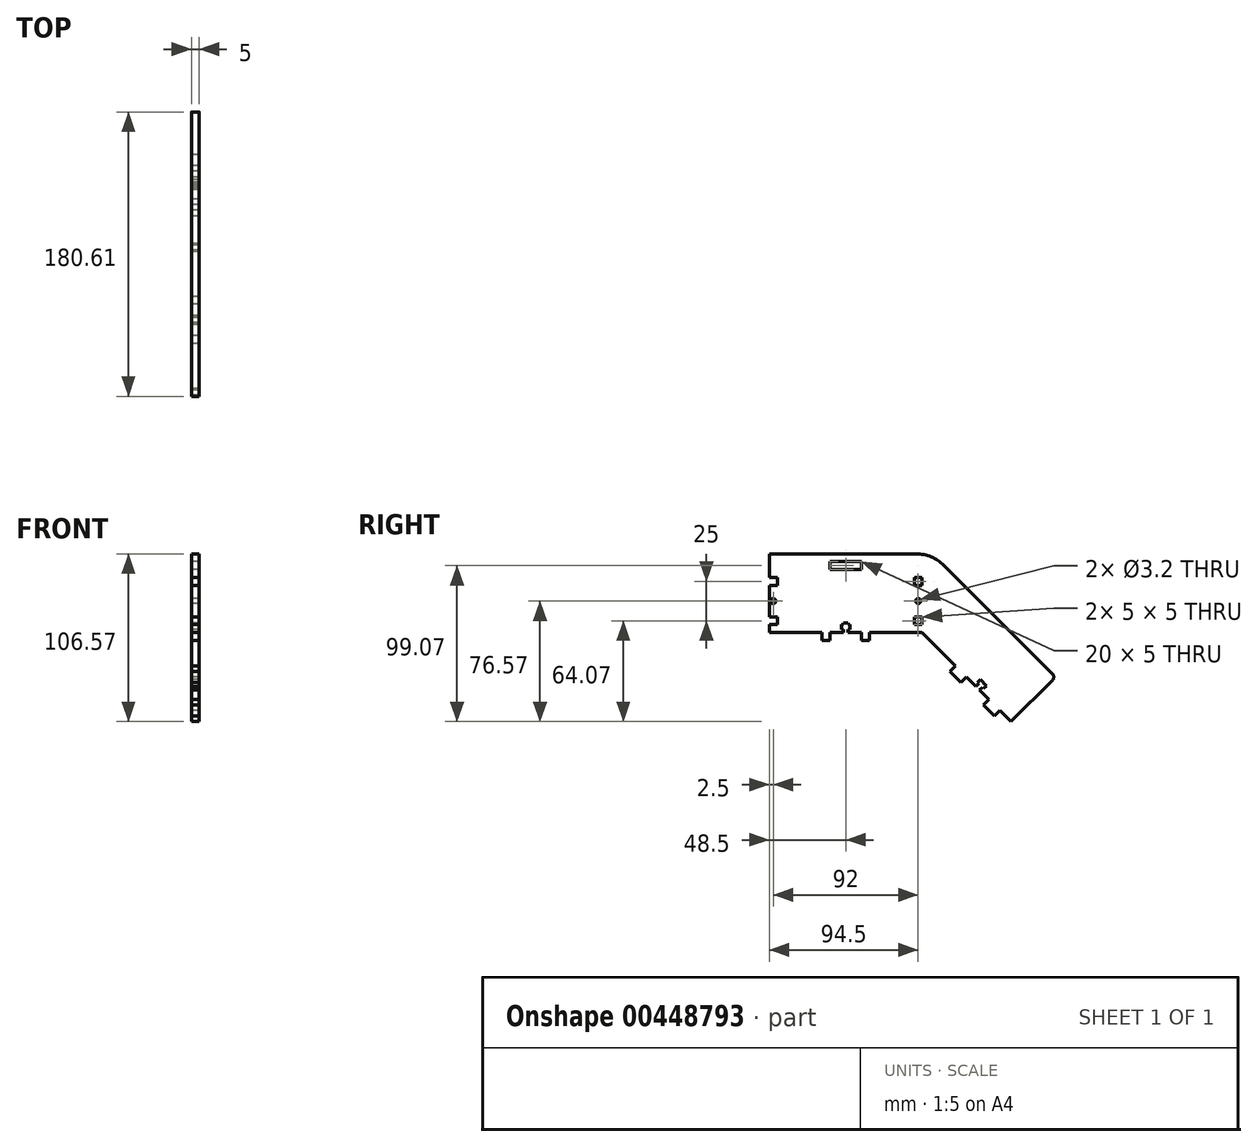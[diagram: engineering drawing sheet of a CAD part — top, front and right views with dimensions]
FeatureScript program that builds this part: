
annotation { "Feature Type Name" : "Feature", "Feature Type Description" : "" }
export const myFeature = defineFeature(function(context is Context, id is Id, definition is map)
    precondition{}
    {
        {
            assignVariable(context, id + "F0", {"name" : "thickness", "anyValue" : 5 * mm});
        }
        {
            var Q0;
            Q0=qCreatedBy(makeId("Right.planeOp"),FACE);
            var sketch = newSketch(context, id + "F1", { "sketchPlane" : qUnion([Q0])});
            skLineSegment(sketch, "E0.bottom", {"start": v(0, 0) * mm, "end": v(33.5, 0) * mm});
            skLineSegment(sketch, "E0.top", {"start": v(0, 40) * mm, "end": v(33.5, 40) * mm, "construction": true});
            skLineSegment(sketch, "E0.left", {"start": v(0, 0) * mm, "end": v(0, 5) * mm});
            skLineSegment(sketch, "E1", {"start": v(33.5, 40) * mm, "end": v(33.5, 45) * mm, "construction": true});
            skLineSegment(sketch, "E2", {"start": v(33.5, 45) * mm, "end": v(38.5, 45) * mm, "construction": true});
            skLineSegment(sketch, "E3", {"start": v(38.5, 45) * mm, "end": v(38.5, 40) * mm});
            skLineSegment(sketch, "E4", {"start": v(58.5, 40) * mm, "end": v(58.5, 45) * mm});
            skLineSegment(sketch, "E5", {"start": v(58.5, 45) * mm, "end": v(63.5, 45) * mm, "construction": true});
            skLineSegment(sketch, "E6", {"start": v(63.5, 45) * mm, "end": v(63.5, 40) * mm, "construction": true});
            skLineSegment(sketch, "E7", {"start": v(0, 20) * mm, "end": v(105.28, 20) * mm, "construction": true});
            skLineSegment(sketch, "E8", {"start": v(48.5, 40) * mm, "end": v(48.5, 0) * mm, "construction": true});
            skLineSegment(sketch, "E9", {"start": v(47, 40) * mm, "end": v(47, 38) * mm, "construction": true});
            skLineSegment(sketch, "E10", {"start": v(47, 38) * mm, "end": v(45.75, 38) * mm, "construction": true});
            skLineSegment(sketch, "E11", {"start": v(45.75, 38) * mm, "end": v(45.75, 35) * mm, "construction": true});
            skLineSegment(sketch, "E12", {"start": v(45.75, 35) * mm, "end": v(47, 35) * mm, "construction": true});
            skLineSegment(sketch, "E13", {"start": v(47, 35) * mm, "end": v(47, 34) * mm, "construction": true});
            skLineSegment(sketch, "E14", {"start": v(47, 34) * mm, "end": v(50, 34) * mm, "construction": true});
            skLineSegment(sketch, "E15", {"start": v(50, 34) * mm, "end": v(50, 35) * mm, "construction": true});
            skLineSegment(sketch, "E16", {"start": v(50, 35) * mm, "end": v(51.25, 35) * mm, "construction": true});
            skLineSegment(sketch, "E17", {"start": v(51.25, 35) * mm, "end": v(51.25, 38) * mm, "construction": true});
            skLineSegment(sketch, "E18", {"start": v(51.25, 38) * mm, "end": v(50, 38) * mm, "construction": true});
            skLineSegment(sketch, "E19", {"start": v(50, 38) * mm, "end": v(50, 40) * mm, "construction": true});
            skPoint(sketch, "E20", {"position": v(48.5, 34) * mm});
            skLineSegment(sketch, "E21.trimOffspring", {"start": v(50, 40) * mm, "end": v(58.5, 40) * mm, "construction": true});
            skLineSegment(sketch, "E22.trimOffspring", {"start": v(38.5, 40) * mm, "end": v(47, 40) * mm, "construction": true});
            skCircle(sketch, "E23", {"center": v(2.5, 20) * mm, "radius": 1.6 * mm});
            skLineSegment(sketch, "E24", {"start": v(0, 35) * mm, "end": v(5, 35) * mm});
            skLineSegment(sketch, "E25", {"start": v(5, 35) * mm, "end": v(5, 30) * mm});
            skLineSegment(sketch, "E26", {"start": v(5, 30) * mm, "end": v(0, 30) * mm});
            skLineSegment(sketch, "E27", {"start": v(0, 10) * mm, "end": v(5, 10) * mm});
            skLineSegment(sketch, "E28", {"start": v(5, 10) * mm, "end": v(5, 5) * mm});
            skLineSegment(sketch, "E29", {"start": v(5, 5) * mm, "end": v(0, 5) * mm});
            skPoint(sketch, "E30", {"position": v(2.5, 30) * mm});
            skLineSegment(sketch, "E31.trimOffspring", {"start": v(0, 35) * mm, "end": v(0, 40) * mm});
            skLineSegment(sketch, "E32.trimOffspring", {"start": v(0, 10) * mm, "end": v(0, 30) * mm});
            skLineSegment(sketch, "E33.trimOffspring", {"start": v(50, 0) * mm, "end": v(58.5, 0) * mm});
            skLineSegment(sketch, "E34.MirrorCS", {"start": v(51.25, 2) * mm, "end": v(50, 2) * mm});
            skLineSegment(sketch, "E35.MirrorCS", {"start": v(50, 6) * mm, "end": v(50, 5) * mm});
            skLineSegment(sketch, "E36.MirrorCS", {"start": v(50, 2) * mm, "end": v(50, 0) * mm});
            skLineSegment(sketch, "E37.MirrorCS", {"start": v(45.75, 5) * mm, "end": v(47, 5) * mm});
            skLineSegment(sketch, "E38.MirrorCS", {"start": v(47, 2) * mm, "end": v(45.75, 2) * mm});
            skLineSegment(sketch, "E39.MirrorCS", {"start": v(50, 5) * mm, "end": v(51.25, 5) * mm});
            skLineSegment(sketch, "E40.MirrorCS", {"start": v(47, 5) * mm, "end": v(47, 6) * mm});
            skLineSegment(sketch, "E41.MirrorCS", {"start": v(47, 0) * mm, "end": v(47, 2) * mm});
            skLineSegment(sketch, "E42.MirrorCS", {"start": v(47, 6) * mm, "end": v(50, 6) * mm});
            skLineSegment(sketch, "E43.MirrorCS", {"start": v(38.5, 0) * mm, "end": v(47, 0) * mm});
            skLineSegment(sketch, "E44.MirrorCS", {"start": v(51.25, 5) * mm, "end": v(51.25, 2) * mm});
            skLineSegment(sketch, "E45.MirrorCS", {"start": v(58.5, -5) * mm, "end": v(63.5, -5) * mm});
            skLineSegment(sketch, "E46.MirrorCS", {"start": v(58.5, 0) * mm, "end": v(58.5, -5) * mm});
            skLineSegment(sketch, "E47.MirrorCS", {"start": v(33.5, 0) * mm, "end": v(33.5, -5) * mm});
            skLineSegment(sketch, "E48.MirrorCS", {"start": v(45.75, 2) * mm, "end": v(45.75, 5) * mm});
            skPoint(sketch, "E49.MirrorP", {"position": v(48.5, 6) * mm});
            skLineSegment(sketch, "E50.MirrorCS", {"start": v(63.5, -5) * mm, "end": v(63.5, 0) * mm});
            skLineSegment(sketch, "E51.MirrorCS", {"start": v(38.5, -5) * mm, "end": v(38.5, 0) * mm});
            skLineSegment(sketch, "E52.MirrorCS", {"start": v(33.5, -5) * mm, "end": v(38.5, -5) * mm});
            skLineSegment(sketch, "E53.trimOffspring", {"start": v(63.5, 0) * mm, "end": v(97, 0) * mm});
            skLineSegment(sketch, "E54", {"start": v(97, 0) * mm, "end": v(131.22, -34.22) * mm});
            skLineSegment(sketch, "E55", {"start": v(153.57, -56.57) * mm, "end": v(179.73, -30.4) * mm});
            skLineSegment(sketch, "E56", {"start": v(179.73, -26.16) * mm, "end": v(110.9, 42.68) * mm});
            skLineSegment(sketch, "E57", {"start": v(63.5, 40) * mm, "end": v(103.57, 40) * mm, "construction": true});
            skLineSegment(sketch, "E58", {"start": v(97, 0) * mm, "end": v(113.57, 40) * mm, "construction": true});
            skLineSegment(sketch, "E59", {"start": v(146.5, -49.5) * mm, "end": v(142.96, -53.03) * mm});
            skLineSegment(sketch, "E60", {"start": v(142.96, -53.03) * mm, "end": v(135.9, -45.96) * mm});
            skLineSegment(sketch, "E61", {"start": v(135.9, -45.96) * mm, "end": v(139.43, -42.43) * mm});
            skLineSegment(sketch, "E62", {"start": v(125.28, -28.28) * mm, "end": v(121.75, -31.82) * mm});
            skLineSegment(sketch, "E63", {"start": v(121.75, -31.82) * mm, "end": v(114.68, -24.75) * mm});
            skLineSegment(sketch, "E64", {"start": v(114.68, -24.75) * mm, "end": v(118.21, -21.21) * mm});
            skLineSegment(sketch, "E65", {"start": v(132.36, -35.36) * mm, "end": v(160.64, -7.07) * mm, "construction": true});
            skLineSegment(sketch, "E66", {"start": v(131.22, -34.22) * mm, "end": v(133, -32.46) * mm});
            skLineSegment(sketch, "E67", {"start": v(133, -32.46) * mm, "end": v(132.18, -31.64) * mm});
            skLineSegment(sketch, "E68", {"start": v(132.18, -31.64) * mm, "end": v(133.95, -29.88) * mm});
            skLineSegment(sketch, "E69", {"start": v(133.95, -29.88) * mm, "end": v(135.9, -31.82) * mm});
            skLineSegment(sketch, "E70.MirrorCS", {"start": v(133.49, -36.49) * mm, "end": v(135.25, -34.72) * mm});
            skLineSegment(sketch, "E71.MirrorCS", {"start": v(135.25, -34.72) * mm, "end": v(136.07, -35.53) * mm});
            skLineSegment(sketch, "E72.MirrorCS", {"start": v(136.07, -35.53) * mm, "end": v(137.84, -33.76) * mm});
            skLineSegment(sketch, "E73.MirrorCS", {"start": v(137.84, -33.76) * mm, "end": v(135.9, -31.82) * mm});
            skLineSegment(sketch, "E74.trimOffspring", {"start": v(133.49, -36.49) * mm, "end": v(153.57, -56.57) * mm});
            skPoint(sketch, "E75.visualSharp", {"position": v(113.57, 40) * mm});
            skPoint(sketch, "E76.visualSharp", {"position": v(181.85, -28.28) * mm});
            skArc(sketch, "E76.filletArc", {"start": v(179.73, -30.4) * mm, "mid": v(180.61, -28.28) * mm, "end": v(179.73, -26.16) * mm});
            skLineSegment(sketch, "E77", {"start": v(0, 40) * mm, "end": v(0, 50) * mm});
            skLineSegment(sketch, "E78", {"start": v(0, 50) * mm, "end": v(93.21, 50) * mm});
            skLineSegment(sketch, "E79", {"start": v(38.5, 45) * mm, "end": v(58.5, 45) * mm});
            skLineSegment(sketch, "E80", {"start": v(38.5, 40) * mm, "end": v(58.5, 40) * mm});
            skLineSegment(sketch, "E81", {"start": v(97, 0) * mm, "end": v(97, 40) * mm, "construction": true});
            skPoint(sketch, "E82.visualSharp", {"position": v(103.57, 50) * mm});
            skArc(sketch, "E82.filletArc", {"start": v(110.9, 42.68) * mm, "mid": v(102.78, 48.1) * mm, "end": v(93.21, 50) * mm});
            skLineSegment(sketch, "E83.bottom", {"start": v(97, 5) * mm, "end": v(92, 5) * mm});
            skLineSegment(sketch, "E83.top", {"start": v(97, 10) * mm, "end": v(92, 10) * mm});
            skLineSegment(sketch, "E83.left", {"start": v(97, 5) * mm, "end": v(97, 10) * mm});
            skLineSegment(sketch, "E83.right", {"start": v(92, 5) * mm, "end": v(92, 10) * mm});
            skCircle(sketch, "E84", {"center": v(94.5, 20) * mm, "radius": 1.6 * mm});
            skPoint(sketch, "E84.centerSnap0", {"position": v(94.5, 10) * mm});
            skPoint(sketch, "E85.MirrorP", {"position": v(94.5, 30) * mm});
            skLineSegment(sketch, "E86.MirrorCS", {"start": v(92, 35) * mm, "end": v(92, 30) * mm});
            skLineSegment(sketch, "E87.MirrorCS", {"start": v(97, 30) * mm, "end": v(92, 30) * mm});
            skLineSegment(sketch, "E88.MirrorCS", {"start": v(97, 35) * mm, "end": v(97, 30) * mm});
            skLineSegment(sketch, "E89.MirrorCS", {"start": v(97, 35) * mm, "end": v(92, 35) * mm});
            skSolve(sketch);
        }
        {
            var Q0;
            Q0=qSketchRegion(id+"F1",true);
            extrude(context, id + "F2", {"entities" : qUnion([Q0]), "depth" : getVariable(context, 'thickness')});
        }
    });
